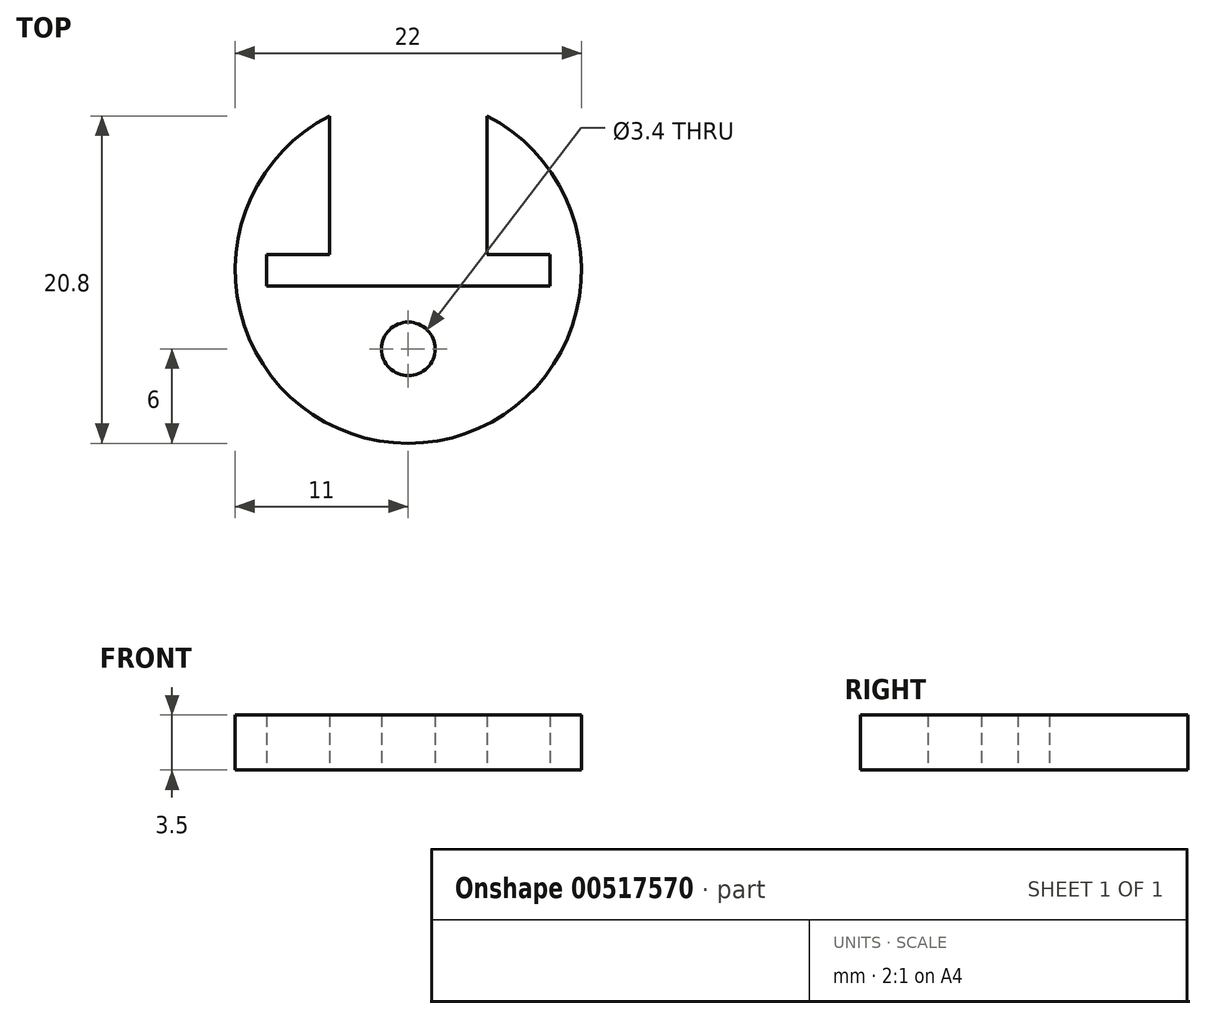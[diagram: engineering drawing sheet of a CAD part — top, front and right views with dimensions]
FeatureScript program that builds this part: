
annotation { "Feature Type Name" : "Feature", "Feature Type Description" : "" }
export const myFeature = defineFeature(function(context is Context, id is Id, definition is map)
    precondition{}
    {
        {
            var Q0;
            Q0=qCreatedBy(makeId("Top.planeOp"),FACE);
            var sketch = newSketch(context, id + "F0", { "sketchPlane" : qUnion([Q0])});
            skCircle(sketch, "E0", {"center": v(0, 0) * mm, "radius": 11 * mm});
            skLineSegment(sketch, "E1", {"start": v(0, 0) * mm, "end": v(0, -5) * mm});
            skCircle(sketch, "E2", {"center": v(0, -5) * mm, "radius": 1.7 * mm});
            skLineSegment(sketch, "E3", {"start": v(0, 0) * mm, "end": v(0, -1) * mm});
            skLineSegment(sketch, "E4.bottom", {"start": v(9, -1) * mm, "end": v(-9, -1) * mm});
            skLineSegment(sketch, "E4.top", {"start": v(9, 1) * mm, "end": v(-9, 1) * mm});
            skLineSegment(sketch, "E4.left", {"start": v(9, -1) * mm, "end": v(9, 1) * mm});
            skLineSegment(sketch, "E4.right", {"start": v(-9, -1) * mm, "end": v(-9, 1) * mm});
            skLineSegment(sketch, "E5", {"start": v(0, 0) * mm, "end": v(0, 5.75) * mm});
            skLineSegment(sketch, "E6.bottom", {"start": v(5, 0) * mm, "end": v(-5, 0) * mm});
            skLineSegment(sketch, "E6.top", {"start": v(5, 11.5) * mm, "end": v(-5, 11.5) * mm});
            skLineSegment(sketch, "E6.left", {"start": v(5, 0) * mm, "end": v(5, 11.5) * mm});
            skLineSegment(sketch, "E6.right", {"start": v(-5, 0) * mm, "end": v(-5, 11.5) * mm});
            skPoint(sketch, "E6.middle", {"position": v(0, 5.75) * mm});
            skSolve(sketch);
        }
        {
            var Q0;
            Q0=makeQuery(id+"F0.imprint","IMPRINT",FACE,{"disambiguationData":[TD([[makeQuery(id+"F0.imprint","IMPRINT",EDGE,{"derivedFrom":sQuery(id+"F0.wireOp",EDGE,"E2")}),-1.0]])]});
            extrude(context, id + "F1", {"entities" : qUnion([Q0]), "depth" : 3.5 * mm, "offsetDistance" : 25 * mm});
        }
    });
